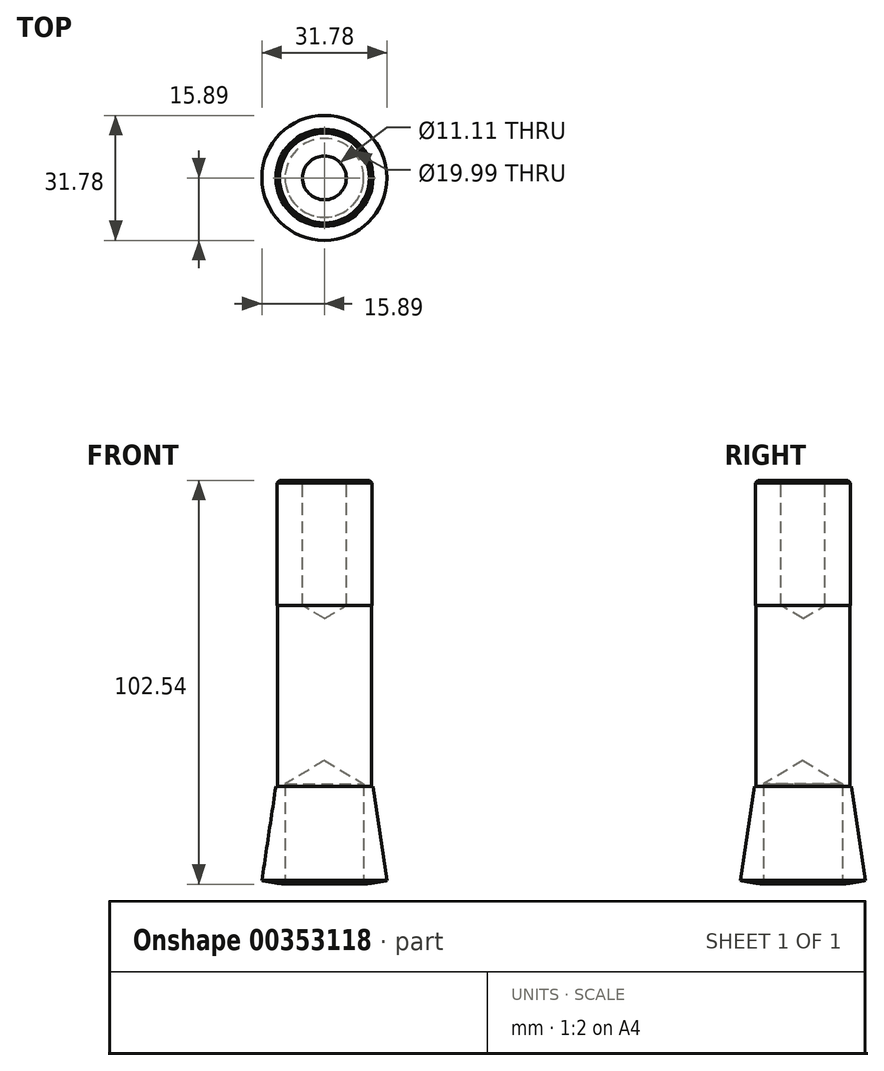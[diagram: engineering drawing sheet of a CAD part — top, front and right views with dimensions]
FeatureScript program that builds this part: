
annotation { "Feature Type Name" : "Feature", "Feature Type Description" : "" }
export const myFeature = defineFeature(function(context is Context, id is Id, definition is map)
    precondition{}
    {
        {
            var Q0;
            Q0=qCreatedBy(makeId("Front.planeOp"),FACE);
            var sketch = newSketch(context, id + "F0", { "sketchPlane" : qUnion([Q0])});
            skLineSegment(sketch, "E0", {"start": v(0, 0) * mm, "end": v(0, 114.3) * mm});
            skPoint(sketch, "E1", {"position": v(-15.88, 0) * mm});
            skLineSegment(sketch, "E2", {"start": v(-15.88, 0) * mm, "end": v(-12.34, 23.88) * mm});
            skLineSegment(sketch, "E3", {"start": v(0, 101.6) * mm, "end": v(-12.05, 101.6) * mm});
            skLineSegment(sketch, "E4", {"start": v(-12.05, 101.6) * mm, "end": v(-12.05, 69.85) * mm});
            skLineSegment(sketch, "E5", {"start": v(-12.05, 69.85) * mm, "end": v(-11.94, 69.85) * mm});
            skLineSegment(sketch, "E6", {"start": v(-11.94, 69.85) * mm, "end": v(-11.94, 26.58) * mm});
            skLineSegment(sketch, "E7", {"start": v(-15.88, 0) * mm, "end": v(0, 0) * mm});
            skLineSegment(sketch, "E8", {"start": v(-12.34, 23.88) * mm, "end": v(-11.94, 23.88) * mm});
            skLineSegment(sketch, "E9", {"start": v(-11.94, 26.58) * mm, "end": v(-11.94, 23.88) * mm});
            skSolve(sketch);
        }
        {
            var Q0;
            Q0 = qSketchRegion(id + "F0", true);
            var Q1;
            Q1=sQuery(id+"F0.wireOp",EDGE,"E0");
            revolve(context, id + "F1", {"entities" : qUnion([Q0]), "axis" : qUnion([Q1]), "revolveType" : RevolveType.FULL});
        }
        {
            var Q0;
            Q0=makeQuery(id+"F1.opRevolve","SWEPT_FACE",FACE,{"disambiguationData":[OSD([sQuery(id+"F0.wireOp",EDGE,"E3")])]});
            var sketch = newSketch(context, id + "F2", { "sketchPlane" : qUnion([Q0])});
            skPoint(sketch, "E10", {"position": v(0, 0) * mm});
            skSolve(sketch);
        }
        {
            var Q0;
            Q0=sQuery(id+"F2.wireOp",VERTEX,"E10");
            var Q1;
            Q1=makeQuery(id+"F1.opRevolve","SWEPT_BODY",BODY,{"disambiguationData":[OSD([sQuery(id+"F0.wireOp",EDGE,"E0"),sQuery(id+"F0.wireOp",EDGE,"E2"),sQuery(id+"F0.wireOp",EDGE,"E3"),sQuery(id+"F0.wireOp",EDGE,"E4"),sQuery(id+"F0.wireOp",EDGE,"E5"),sQuery(id+"F0.wireOp",EDGE,"E6"),sQuery(id+"F0.wireOp",EDGE,"E7"),sQuery(id+"F0.wireOp",EDGE,"E8"),sQuery(id+"F0.wireOp",EDGE,"E9")])]});
            hole(context, id + "F3", {"style" : HoleStyle.SIMPLE, "endStyle" : HoleEndStyle.BLIND, "holeDiameter" : 11.1 * mm, "holeDepth" : 31.75 * mm, "isTappedThrough" : true, "tappedDepth" : 12.7 * mm, "tapClearance" : 3, "locations" : qUnion([Q0]), "scope" : qUnion([Q1])});
        }
        {
            var Q0;
            Q0=makeQuery(id+"F1.opRevolve","SWEPT_EDGE",EDGE,{"disambiguationData":[OSD([sQuery(id+"F0.wireOp",EDGE,"E3"),sQuery(id+"F0.wireOp",EDGE,"E4")])]});
            chamfer(context, id + "F4", {"entities" : qUnion([Q0]), "width" : 0.64 * mm, "tangentPropagation" : true});
        }
        {
            var Q0;
            Q0=qCreatedBy(makeId("Right.planeOp"),FACE);
            var sketch = newSketch(context, id + "F5", { "sketchPlane" : qUnion([Q0])});
            skArc(sketch, "E11", {"start": v(0, -1.54) * mm, "mid": v(7.98, -1.16) * mm, "end": v(15.9, 0) * mm});
            skLineSegment(sketch, "E12", {"start": v(0, 0) * mm, "end": v(0, -3) * mm});
            skPoint(sketch, "E13", {"position": v(15.9, 0) * mm});
            skLineSegment(sketch, "E14", {"start": v(15.9, 0) * mm, "end": v(0, 0) * mm});
            skSolve(sketch);
        }
        {
            var Q0;
            {var subQ0=sQuery(id+"F5.wireOp",EDGE,"E11");Q0=makeQuery(id+"F5.imprint","IMPRINT",FACE,{"disambiguationData":[TD([[makeQuery(id+"F5.imprint","IMPRINT",EDGE,{"derivedFrom":subQ0}),1.0]])]});}
            var Q1;
            Q1=sQuery(id+"F5.wireOp",EDGE,"E12");
            revolve(context, id + "F6", {"operationType" : NewBodyOperationType.ADD, "entities" : qUnion([Q0]), "axis" : qUnion([Q1]), "revolveType" : RevolveType.FULL});
        }
        {
            var Q0;
            Q0=qCreatedBy(makeId("Top.planeOp"),FACE);
            cPlane(context, id + "F7", {"entities" : qUnion([Q0]), "cplaneType" : CPlaneType.OFFSET, "offset" : 3.3 * mm, "oppositeDirection" : true, "width" : 152.4 * mm, "height" : 152.4 * mm});
        }
        {
            var Q0;
            Q0=qCreatedBy(id+"F7.planeOp",FACE);
            var sketch = newSketch(context, id + "F8", { "sketchPlane" : qUnion([Q0])});
            skPoint(sketch, "E15", {"position": v(0, 0) * mm});
            skSolve(sketch);
        }
        {
            var Q0;
            Q0=sQuery(id+"F8.wireOp",VERTEX,"E15");
            var Q1;
            Q1=makeQuery(id+"F1.opRevolve","SWEPT_BODY",BODY,{"disambiguationData":[OSD([sQuery(id+"F0.wireOp",EDGE,"E0"),sQuery(id+"F0.wireOp",EDGE,"E2"),sQuery(id+"F0.wireOp",EDGE,"E3"),sQuery(id+"F0.wireOp",EDGE,"E4"),sQuery(id+"F0.wireOp",EDGE,"E5"),sQuery(id+"F0.wireOp",EDGE,"E6"),sQuery(id+"F0.wireOp",EDGE,"E7"),sQuery(id+"F0.wireOp",EDGE,"E8"),sQuery(id+"F0.wireOp",EDGE,"E9")])]});
            hole(context, id + "F9", {"style" : HoleStyle.SIMPLE, "endStyle" : HoleEndStyle.BLIND, "oppositeDirection" : true, "holeDiameter" : 19.99 * mm, "holeDepth" : 25.4 * mm, "isTappedThrough" : true, "tappedDepth" : 12.7 * mm, "tapClearance" : 3, "locations" : qUnion([Q0]), "scope" : qUnion([Q1])});
        }
    });
